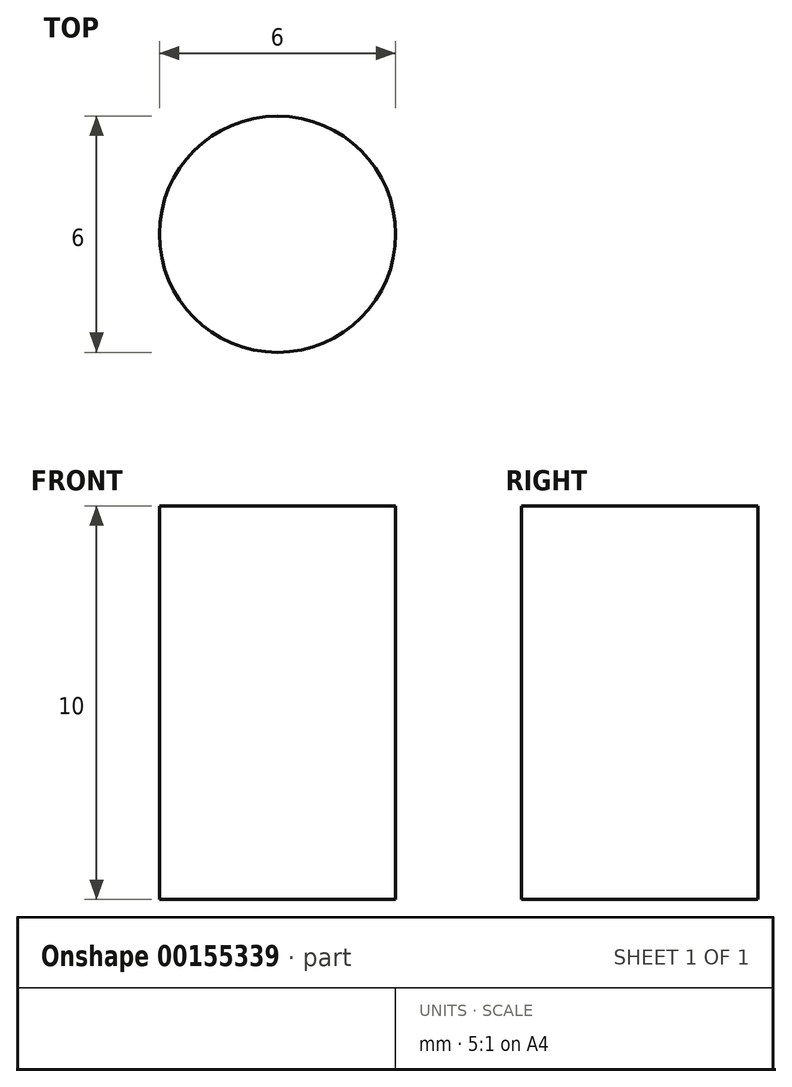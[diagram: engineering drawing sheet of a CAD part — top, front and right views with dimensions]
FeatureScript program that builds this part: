
annotation { "Feature Type Name" : "Feature", "Feature Type Description" : "" }
export const myFeature = defineFeature(function(context is Context, id is Id, definition is map)
    precondition{}
    {
        {
            var Q0;
            Q0=qCreatedBy(makeId("Top.planeOp"),FACE);
            var sketch = newSketch(context, id + "F0", { "sketchPlane" : qUnion([Q0])});
            skCircle(sketch, "E0", {"center": v(0, 0) * mm, "radius": 3 * mm});
            skSolve(sketch);
        }
        {
            var Q0;
            Q0 = qSketchRegion(id + "F0", true);
            extrude(context, id + "F1", {"entities" : qUnion([Q0]), "depth" : 10 * mm});
        }
    });
